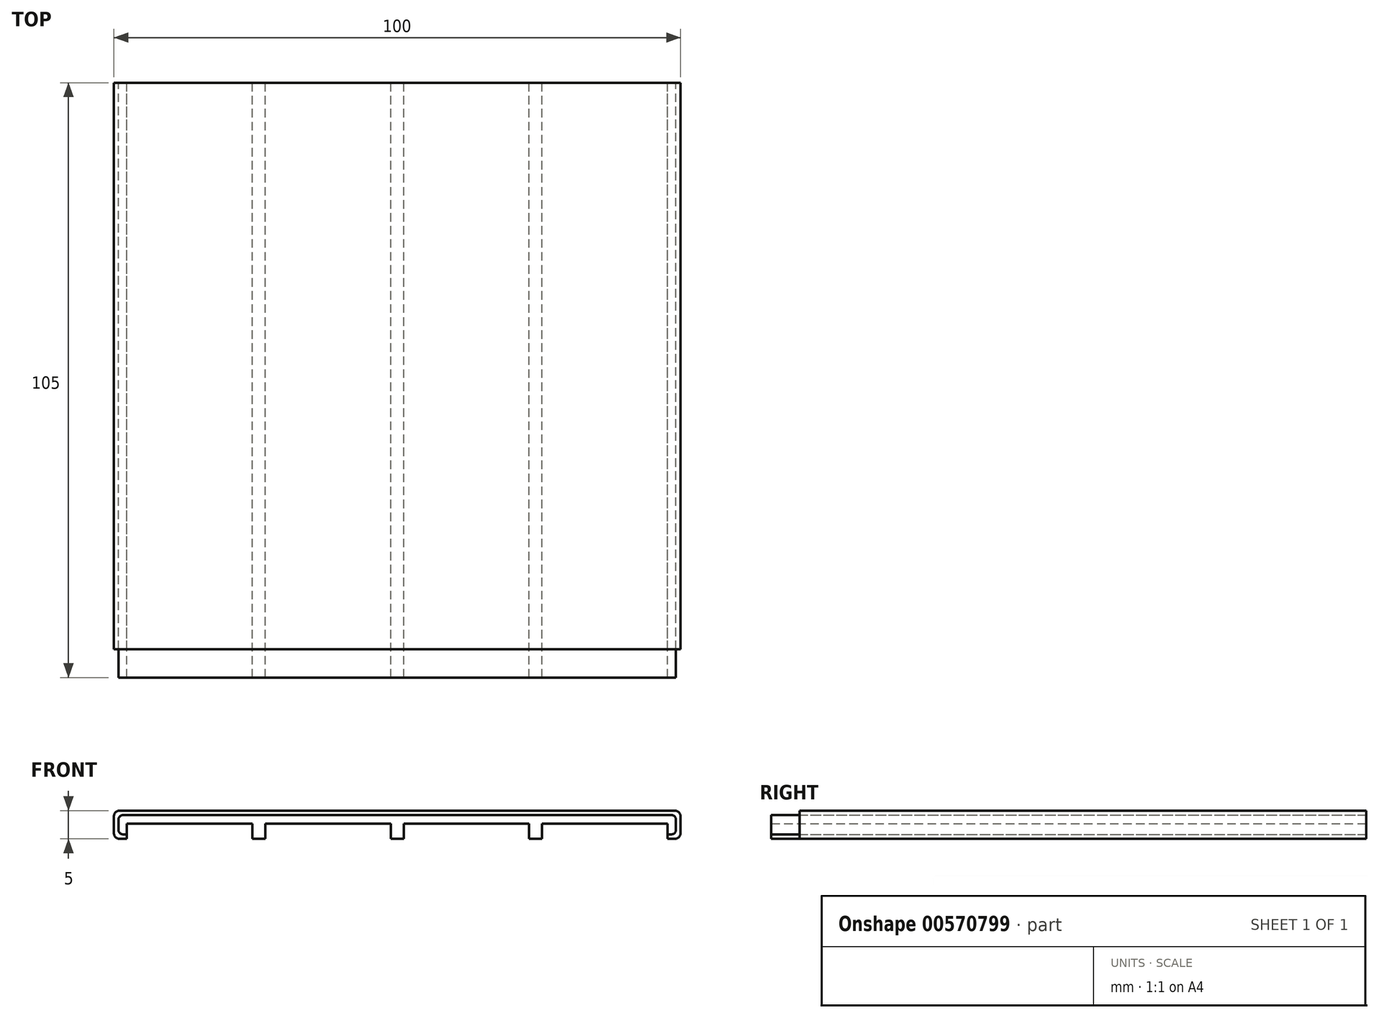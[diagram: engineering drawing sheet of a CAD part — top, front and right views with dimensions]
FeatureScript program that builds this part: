
annotation { "Feature Type Name" : "Feature", "Feature Type Description" : "" }
export const myFeature = defineFeature(function(context is Context, id is Id, definition is map)
    precondition{}
    {
        {
            var Q0;
            Q0=qCreatedBy(makeId("Front.planeOp"),FACE);
            var sketch = newSketch(context, id + "F0", { "sketchPlane" : qUnion([Q0])});
            skLineSegment(sketch, "E0.bottom", {"start": v(50, -2.5) * mm, "end": v(49.2, -2.5) * mm});
            skLineSegment(sketch, "E0.top", {"start": v(49, 2.5) * mm, "end": v(-49, 2.5) * mm});
            skLineSegment(sketch, "E0.left", {"start": v(50, -1.5) * mm, "end": v(50, 1.5) * mm});
            skLineSegment(sketch, "E0.right", {"start": v(-50, -1.5) * mm, "end": v(-50, 1.5) * mm});
            skPoint(sketch, "E0.middle", {"position": v(0, 0) * mm});
            skLineSegment(sketch, "E1", {"start": v(-48.4, 1.7) * mm, "end": v(48.4, 1.7) * mm});
            skLineSegment(sketch, "E2", {"start": v(-49.2, 0.9) * mm, "end": v(-49.2, -0.9) * mm});
            skLineSegment(sketch, "E3", {"start": v(49.2, 0.9) * mm, "end": v(49.2, -0.9) * mm});
            skPoint(sketch, "E4.orphan", {"position": v(49.2, -2.5) * mm});
            skLineSegment(sketch, "E5", {"start": v(-49.2, -2.5) * mm, "end": v(-49.2, -2.5) * mm});
            skLineSegment(sketch, "E6.trimOffspring", {"start": v(-49.2, -2.5) * mm, "end": v(-50, -2.5) * mm});
            skLineSegment(sketch, "E7", {"start": v(49.2, -2.5) * mm, "end": v(49.2, -2.5) * mm});
            skLineSegment(sketch, "E8.0", {"start": v(-47.7, 0.2) * mm, "end": v(-47.7, -2.5) * mm});
            skLineSegment(sketch, "E8.1", {"start": v(-47.7, 0.2) * mm, "end": v(-25.57, 0.2) * mm});
            skLineSegment(sketch, "E8.2", {"start": v(47.7, 0.2) * mm, "end": v(47.7, -2.5) * mm});
            skLineSegment(sketch, "E9", {"start": v(-50, -2.5) * mm, "end": v(-47.7, -2.5) * mm});
            skLineSegment(sketch, "E10", {"start": v(-1.15, 0.2) * mm, "end": v(-1.15, -2.5) * mm});
            skLineSegment(sketch, "E11", {"start": v(-1.15, -2.5) * mm, "end": v(1.15, -2.5) * mm});
            skLineSegment(sketch, "E12", {"start": v(1.15, -2.5) * mm, "end": v(1.15, 0.2) * mm});
            skLineSegment(sketch, "E13", {"start": v(-25.57, 0.2) * mm, "end": v(-25.57, -2.5) * mm});
            skLineSegment(sketch, "E14", {"start": v(-25.57, -2.5) * mm, "end": v(-23.28, -2.5) * mm});
            skLineSegment(sketch, "E15", {"start": v(-23.28, -2.5) * mm, "end": v(-23.28, 0.2) * mm});
            skLineSegment(sketch, "E16", {"start": v(49, -2.5) * mm, "end": v(47.7, -2.5) * mm});
            skLineSegment(sketch, "E17", {"start": v(23.28, 0.2) * mm, "end": v(23.28, -2.5) * mm});
            skLineSegment(sketch, "E18", {"start": v(25.58, 0.2) * mm, "end": v(25.58, -2.5) * mm});
            skLineSegment(sketch, "E19.trimOffspring", {"start": v(1.15, 0.2) * mm, "end": v(23.28, 0.2) * mm});
            skPoint(sketch, "E20.start.orphan", {"position": v(0, -0.8) * mm});
            skPoint(sketch, "E21.start.orphan", {"position": v(0, -0.94) * mm});
            skLineSegment(sketch, "E22.trimOffspring", {"start": v(-23.28, 0.2) * mm, "end": v(-1.15, 0.2) * mm});
            skLineSegment(sketch, "E23.trimOffspring", {"start": v(25.58, 0.2) * mm, "end": v(47.7, 0.2) * mm});
            skLineSegment(sketch, "E24", {"start": v(-48.4, -1.7) * mm, "end": v(-47.7, -1.7) * mm});
            skLineSegment(sketch, "E25", {"start": v(48.4, -1.7) * mm, "end": v(47.7, -1.7) * mm});
            skLineSegment(sketch, "E26.trimOffspring", {"start": v(-47.7, -2.5) * mm, "end": v(-49, -2.5) * mm});
            skLineSegment(sketch, "E27.trimOffspring", {"start": v(-23.28, -2.5) * mm, "end": v(-25.57, -2.5) * mm});
            skLineSegment(sketch, "E28.trimOffspring", {"start": v(1.15, -2.5) * mm, "end": v(-1.15, -2.5) * mm});
            skLineSegment(sketch, "E29.trimOffspring", {"start": v(25.58, -2.5) * mm, "end": v(23.28, -2.5) * mm});
            skPoint(sketch, "E30.visualSharp", {"position": v(-50, 2.5) * mm});
            skArc(sketch, "E30.filletArc", {"start": v(-49, 2.5) * mm, "mid": v(-49.7, 2.2) * mm, "end": v(-50, 1.5) * mm});
            skPoint(sketch, "E31.visualSharp", {"position": v(-50, -2.5) * mm});
            skArc(sketch, "E31.filletArc", {"start": v(-50, -1.5) * mm, "mid": v(-49.7, -2.2) * mm, "end": v(-49, -2.5) * mm});
            skPoint(sketch, "E32.visualSharp", {"position": v(50, 2.5) * mm});
            skArc(sketch, "E32.filletArc", {"start": v(50, 1.5) * mm, "mid": v(49.7, 2.2) * mm, "end": v(49, 2.5) * mm});
            skPoint(sketch, "E33.visualSharp", {"position": v(50, -2.5) * mm});
            skArc(sketch, "E33.filletArc", {"start": v(49, -2.5) * mm, "mid": v(49.7, -2.2) * mm, "end": v(50, -1.5) * mm});
            skPoint(sketch, "E34.visualSharp", {"position": v(49.2, -1.7) * mm});
            skArc(sketch, "E34.filletArc", {"start": v(48.4, -1.7) * mm, "mid": v(48.97, -1.47) * mm, "end": v(49.2, -0.9) * mm});
            skPoint(sketch, "E35.visualSharp", {"position": v(49.2, 1.7) * mm});
            skArc(sketch, "E35.filletArc", {"start": v(49.2, 0.9) * mm, "mid": v(48.97, 1.47) * mm, "end": v(48.4, 1.7) * mm});
            skPoint(sketch, "E36.visualSharp", {"position": v(-49.2, 1.7) * mm});
            skArc(sketch, "E36.filletArc", {"start": v(-48.4, 1.7) * mm, "mid": v(-48.97, 1.47) * mm, "end": v(-49.2, 0.9) * mm});
            skPoint(sketch, "E37.visualSharp", {"position": v(-49.2, -1.7) * mm});
            skArc(sketch, "E37.filletArc", {"start": v(-49.2, -0.9) * mm, "mid": v(-48.97, -1.47) * mm, "end": v(-48.4, -1.7) * mm});
            skSolve(sketch);
        }
        {
            var Q0;
            Q0=makeQuery(id+"F0.imprint","IMPRINT",FACE,{"disambiguationData":[TD([[makeQuery(id+"F0.imprint","IMPRINT",EDGE,{"derivedFrom":sQuery(id+"F0.wireOp",EDGE,"E0.top")}),1.0]])]});
            extrude(context, id + "F1", {"entities" : qUnion([Q0]), "depth" : 100 * mm, "offsetDistance" : 25 * mm});
        }
        {
            var Q0;
            Q0=makeQuery(id+"F0.imprint","IMPRINT",FACE,{"disambiguationData":[TD([[makeQuery(id+"F0.imprint","IMPRINT",EDGE,{"derivedFrom":sQuery(id+"F0.wireOp",EDGE,"E1")}),-1.0]])]});
            extrude(context, id + "F2", {"entities" : qUnion([Q0]), "depth" : 105 * mm, "offsetDistance" : 25 * mm});
        }
    });
